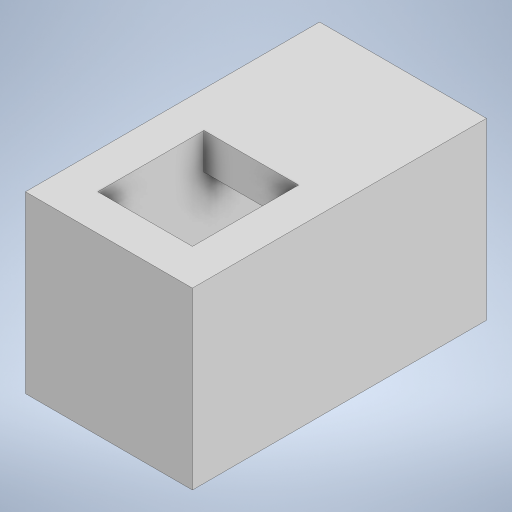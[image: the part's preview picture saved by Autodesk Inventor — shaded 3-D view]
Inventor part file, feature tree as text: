
AUTODESK INVENTOR PART (.ipt)
format: ipt  version: 2024.2 (Build 282272000, 272)  size: 192,000 bytes
history: native  units: in
note: dims shown in document units (in); Inventor stores cm internally (conversion verified against a paired STEP export)
features: sketch x4, extrude x3
ambient origin geometry x8: Origin, YZ Plane, XZ Plane, XY Plane, X Axis, Y Axis, Z Axis, Center Point
bodies: Solid1 (feature_tree)
feature tree (7):
  sketch  "Sketch1"  dims[d0=0.5157in d1=1.2087in]
  extrude  "Extrusion1"  Depth=1.2087in
  extrude  "Extrusion2"  Depth=1.6024in
  extrude  "Extrusion3"  Depth=0.1969in TaperAngle=0.0deg
  sketch  "Sketch2"  dims[d2=0.9094in d3=1.6024in]
  sketch  "Sketch3"  dims[d4=0.7559in d5=0.0in d6=0.1969in d7=0.0in]
  sketch  "Sketch4"  dims[d8=0.5787in d9=0.1969in d10=0.0in]
